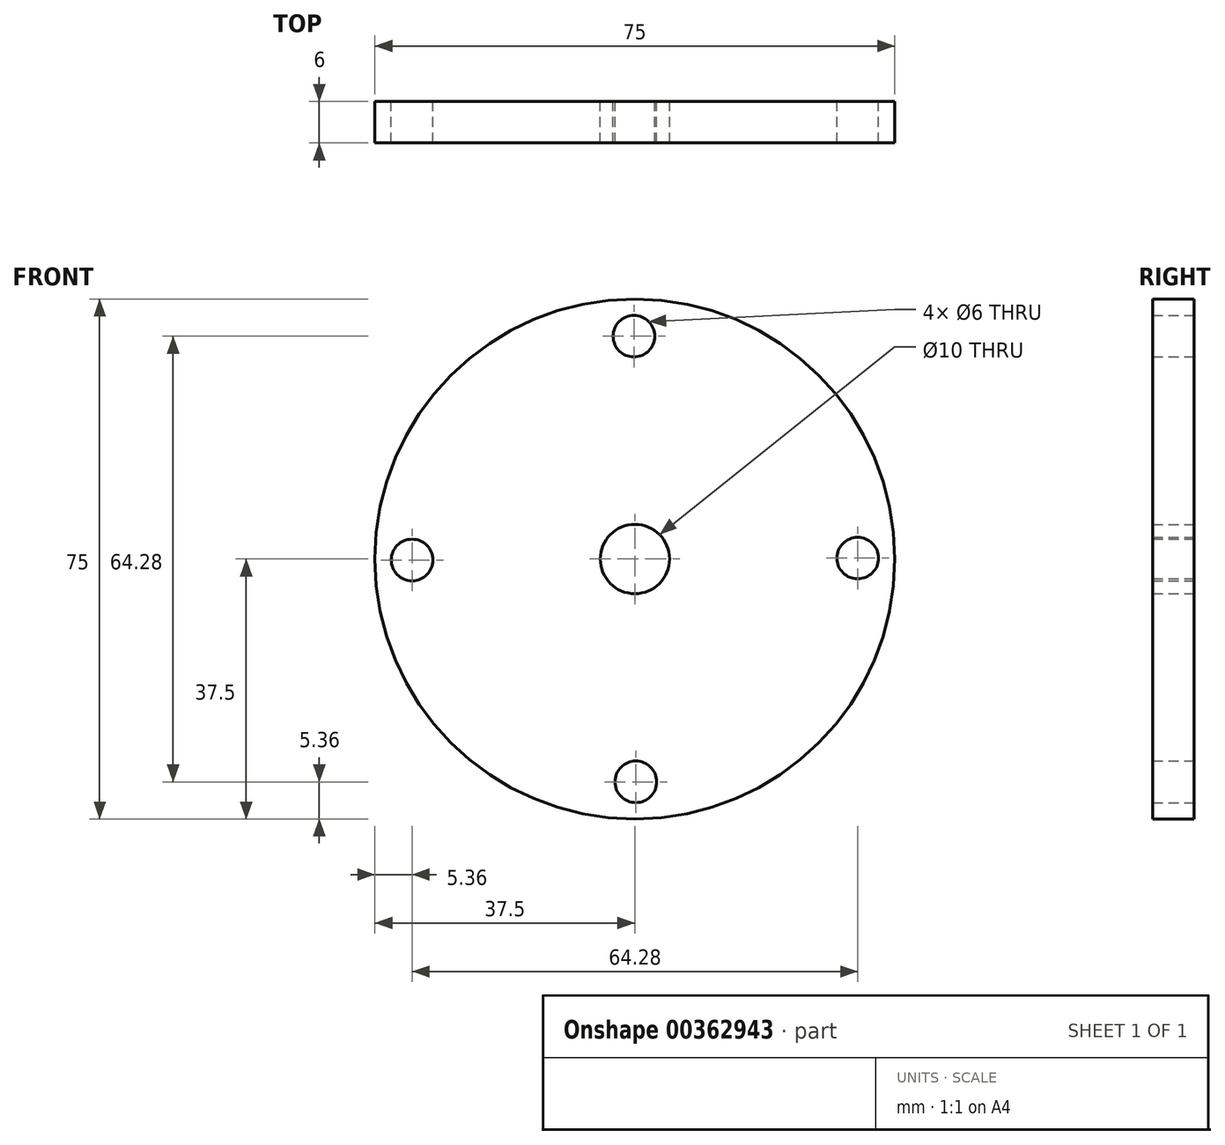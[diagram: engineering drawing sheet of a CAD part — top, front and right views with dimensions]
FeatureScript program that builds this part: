
annotation { "Feature Type Name" : "Feature", "Feature Type Description" : "" }
export const myFeature = defineFeature(function(context is Context, id is Id, definition is map)
    precondition{}
    {
        {
            var Q0;
            Q0=qCreatedBy(makeId("Front.planeOp"),FACE);
            var sketch = newSketch(context, id + "F0", { "sketchPlane" : qUnion([Q0])});
            skCircle(sketch, "E0", {"center": v(0.14, 30) * mm, "radius": 5 * mm});
            skLineSegment(sketch, "E1", {"start": v(0.14, 50.5) * mm, "end": v(0.14, 30) * mm, "construction": true});
            skCircle(sketch, "E2", {"center": v(0.14, 30) * mm, "radius": 37.5 * mm});
            skCircle(sketch, "E3", {"center": v(-0.3, 29.8) * mm, "radius": 12.5 * mm, "construction": true});
            skCircle(sketch, "E4", {"center": v(0, 62.14) * mm, "radius": 3 * mm});
            skCircle(sketch, "E5.1.0", {"center": v(32.28, 30.14) * mm, "radius": 3 * mm});
            skCircle(sketch, "E5.2.0", {"center": v(0.28, -2.14) * mm, "radius": 3 * mm});
            skCircle(sketch, "E5.3.0", {"center": v(-32, 29.86) * mm, "radius": 3 * mm});
            skLineSegment(sketch, "E5.anchor1", {"start": v(0.14, 30) * mm, "end": v(0, 62.14) * mm, "construction": true});
            skLineSegment(sketch, "E5.anchor2", {"start": v(0.14, 30) * mm, "end": v(-32, 29.86) * mm, "construction": true});
            skSolve(sketch);
        }
        {
            var Q0;
            Q0=makeQuery(id+"F0.imprint","IMPRINT",FACE,{"disambiguationData":[TD([[makeQuery(id+"F0.imprint","IMPRINT",EDGE,{"derivedFrom":sQuery(id+"F0.wireOp",EDGE,"xoFEEAgA-wCx4-S8Lq-esRj-uuQ3L0FwZVM2.bottom")}),-1.0]])]});
            var Q1;
            Q1=makeQuery(id+"F0.imprint","IMPRINT",FACE,{"disambiguationData":[TD([[makeQuery(id+"F0.imprint","IMPRINT",EDGE,{"derivedFrom":sQuery(id+"F0.wireOp",EDGE,"E0")}),-1.0]])]});
            extrude(context, id + "F1", {"entities" : qUnion([Q0, Q1]), "depth" : 6 * mm});
        }
    });
